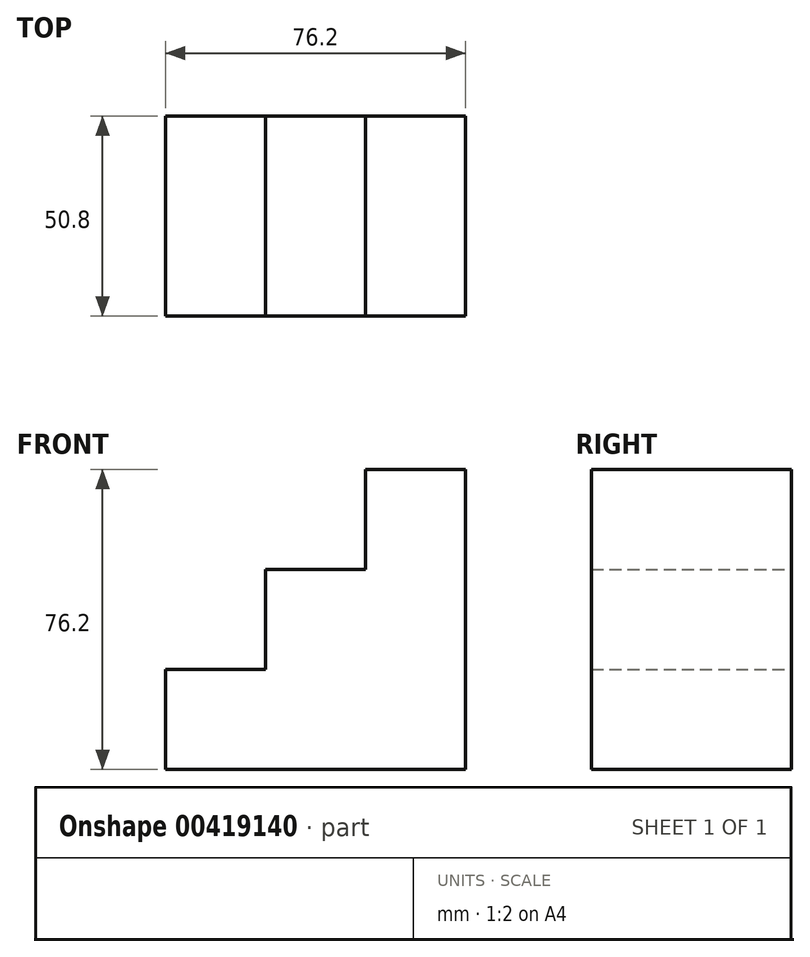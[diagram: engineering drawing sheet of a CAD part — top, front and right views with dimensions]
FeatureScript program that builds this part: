
annotation { "Feature Type Name" : "Feature", "Feature Type Description" : "" }
export const myFeature = defineFeature(function(context is Context, id is Id, definition is map)
    precondition{}
    {
        {
            var Q0;
            Q0=qCreatedBy(makeId("Front.planeOp"),FACE);
            var sketch = newSketch(context, id + "F0", { "sketchPlane" : qUnion([Q0])});
            skLineSegment(sketch, "E0", {"start": v(0, 0) * mm, "end": v(38.1, 0) * mm});
            skLineSegment(sketch, "E1", {"start": v(38.1, 0) * mm, "end": v(0, 0) * mm});
            skLineSegment(sketch, "E2", {"start": v(0, 0) * mm, "end": v(-38.1, 0) * mm});
            skLineSegment(sketch, "E3", {"start": v(-38.1, 0) * mm, "end": v(-38.1, 25.4) * mm});
            skLineSegment(sketch, "E4", {"start": v(-38.1, 25.4) * mm, "end": v(-12.7, 25.4) * mm});
            skLineSegment(sketch, "E5", {"start": v(-12.7, 25.4) * mm, "end": v(-12.7, 50.8) * mm});
            skLineSegment(sketch, "E6", {"start": v(-12.7, 50.8) * mm, "end": v(12.7, 50.8) * mm});
            skLineSegment(sketch, "E7", {"start": v(12.7, 50.8) * mm, "end": v(12.7, 76.2) * mm});
            skLineSegment(sketch, "E8", {"start": v(12.7, 76.2) * mm, "end": v(38.1, 76.2) * mm});
            skLineSegment(sketch, "E9", {"start": v(38.1, 76.2) * mm, "end": v(38.1, 0) * mm});
            skSolve(sketch);
        }
        {
            var Q0;
            Q0 = qSketchRegion(id + "F0", true);
            extrude(context, id + "F1", {"entities" : qUnion([Q0]), "depth" : 50.8 * mm});
        }
    });
